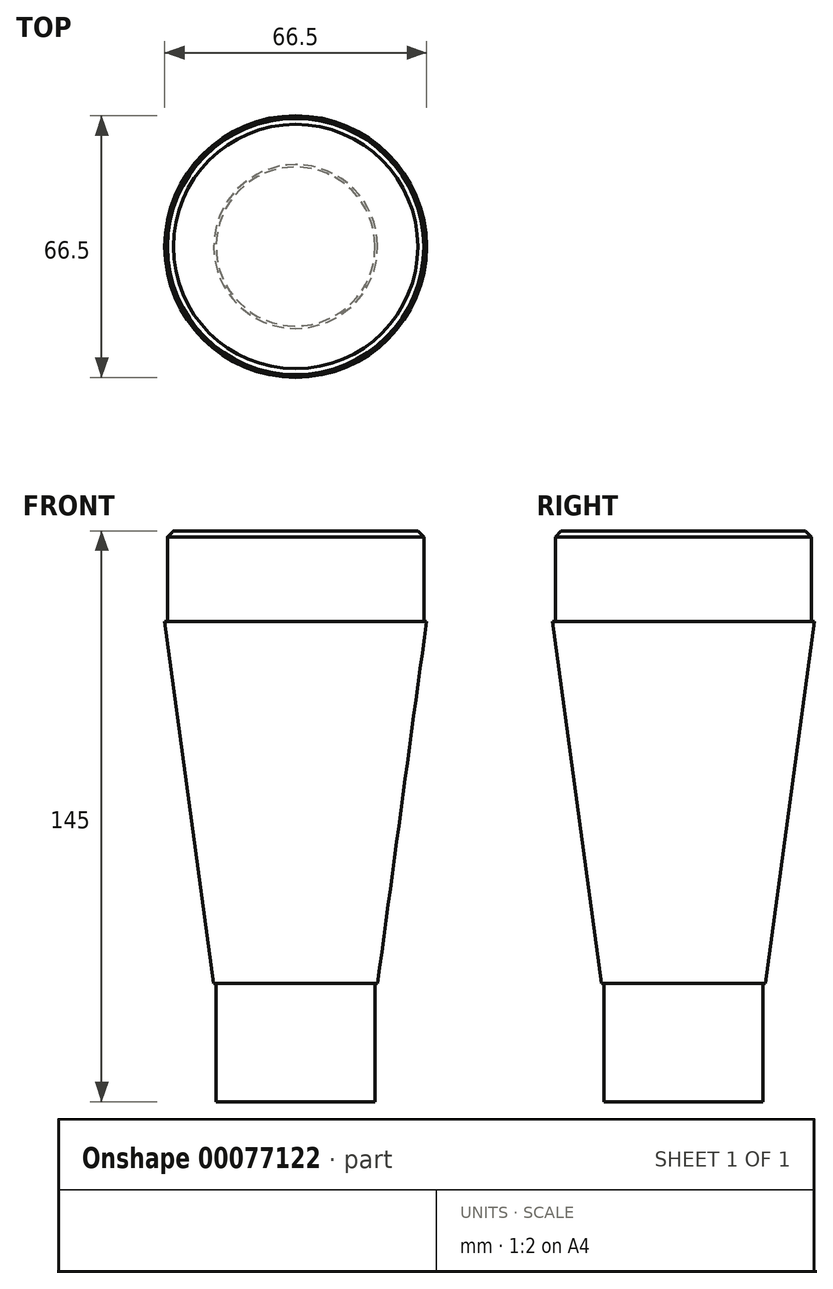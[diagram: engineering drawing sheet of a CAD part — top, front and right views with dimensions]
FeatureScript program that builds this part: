
annotation { "Feature Type Name" : "Feature", "Feature Type Description" : "" }
export const myFeature = defineFeature(function(context is Context, id is Id, definition is map)
    precondition{}
    {
        {
            var Q0;
            Q0=qCreatedBy(makeId("Front.planeOp"),FACE);
            var sketch = newSketch(context, id + "F0", { "sketchPlane" : qUnion([Q0])});
            skLineSegment(sketch, "E0", {"start": v(-32.55, 66.27) * mm, "end": v(-32.55, 43.27) * mm});
            skLineSegment(sketch, "E1", {"start": v(-32.55, 43.27) * mm, "end": v(-33.25, 43.27) * mm});
            skLineSegment(sketch, "E2", {"start": v(-33.25, 43.27) * mm, "end": v(-20.8, -48.73) * mm});
            skLineSegment(sketch, "E3", {"start": v(-20.8, -48.73) * mm, "end": v(-20.2, -48.73) * mm});
            skLineSegment(sketch, "E4", {"start": v(-20.2, -48.73) * mm, "end": v(-20.2, -78.73) * mm});
            skLineSegment(sketch, "E5", {"start": v(-20.2, -78.73) * mm, "end": v(0, -78.73) * mm});
            skLineSegment(sketch, "E6", {"start": v(-32.55, 66.27) * mm, "end": v(0, 66.27) * mm});
            skLineSegment(sketch, "E7", {"start": v(0, 94.78) * mm, "end": v(0, -99.97) * mm, "construction": true});
            skLineSegment(sketch, "E8", {"start": v(0, 66.27) * mm, "end": v(0, -78.73) * mm});
            skSolve(sketch);
        }
        {
            var Q0;
            Q0=makeQuery(id+"F0.imprint","IMPRINT",FACE,{"disambiguationData":[TD([[makeQuery(id+"F0.imprint","IMPRINT",EDGE,{"derivedFrom":sQuery(id+"F0.wireOp",EDGE,"E0")}),1.0]])]});
            var Q1;
            Q1=sQuery(id+"F0.wireOp",EDGE,"E7");
            revolve(context, id + "F1", {"entities" : qUnion([Q0]), "axis" : qUnion([Q1]), "revolveType" : RevolveType.FULL});
        }
        {
            var Q0;
            Q0=makeQuery(id+"F1.opRevolve","SWEPT_EDGE",EDGE,{"disambiguationData":[OSD([sQuery(id+"F0.wireOp",EDGE,"E0"),sQuery(id+"F0.wireOp",EDGE,"E6")])]});
            chamfer(context, id + "F2", {"entities" : qUnion([Q0]), "width" : 1.5 * mm, "tangentPropagation" : true});
        }
    });
